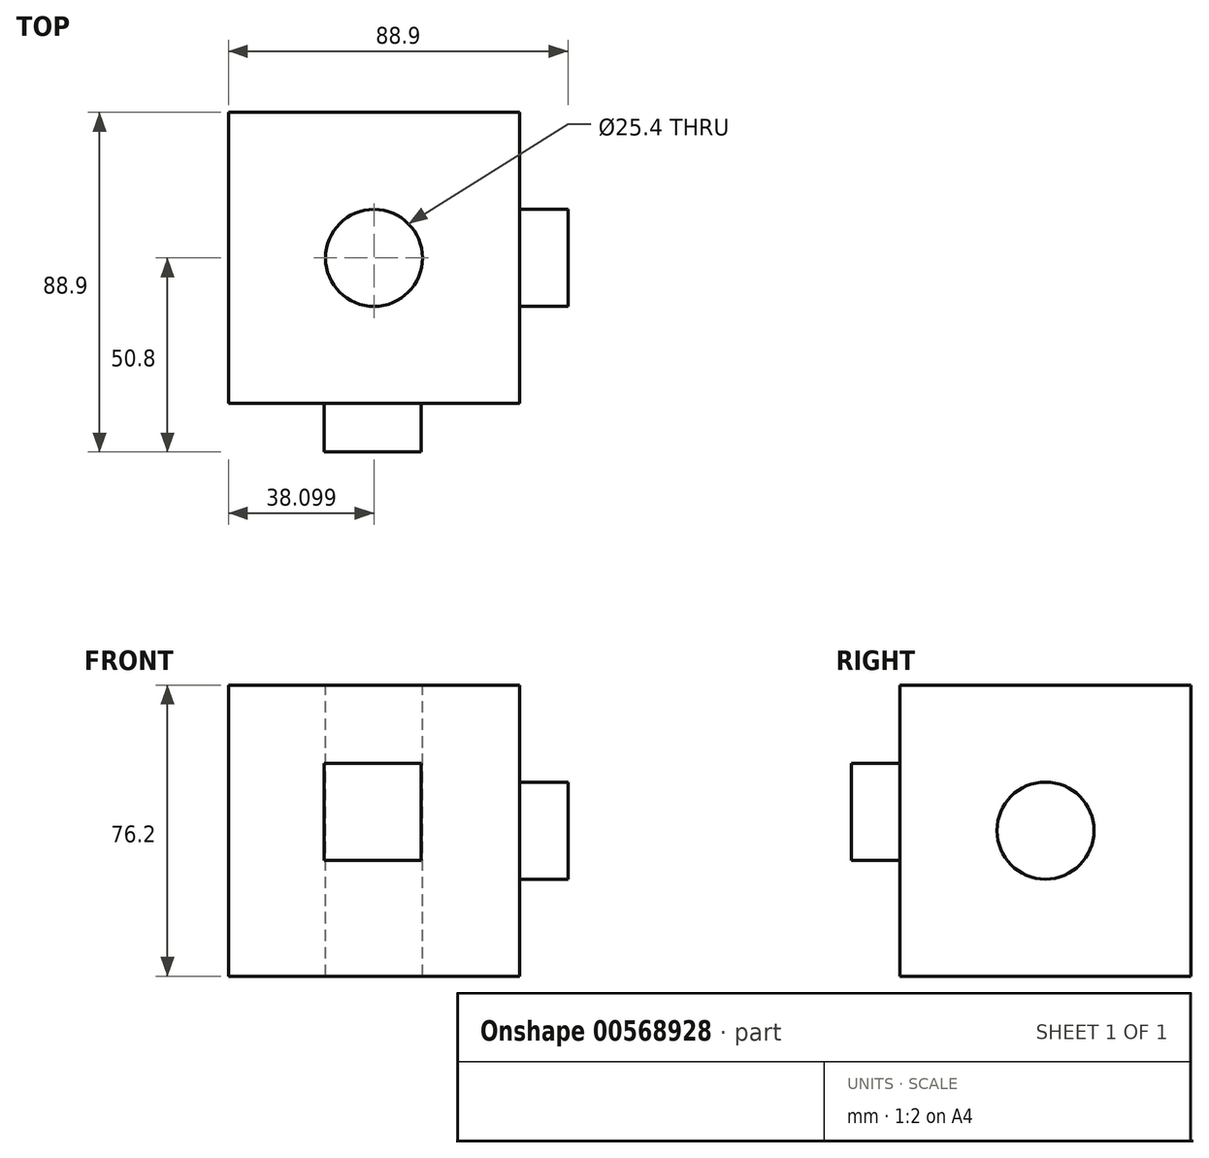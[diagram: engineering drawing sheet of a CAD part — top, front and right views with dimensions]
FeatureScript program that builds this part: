
annotation { "Feature Type Name" : "Feature", "Feature Type Description" : "" }
export const myFeature = defineFeature(function(context is Context, id is Id, definition is map)
    precondition{}
    {
        {
            var Q0;
            Q0=qCreatedBy(makeId("Front.planeOp"),FACE);
            var sketch = newSketch(context, id + "F0", { "sketchPlane" : qUnion([Q0])});
            skLineSegment(sketch, "E0.bottom", {"start": v(76.3, 85.32) * mm, "end": v(0.1, 85.32) * mm});
            skLineSegment(sketch, "E0.top", {"start": v(76.3, 9.12) * mm, "end": v(0.1, 9.12) * mm});
            skLineSegment(sketch, "E0.left", {"start": v(76.3, 85.32) * mm, "end": v(76.3, 9.12) * mm});
            skLineSegment(sketch, "E0.right", {"start": v(0.1, 85.32) * mm, "end": v(0.1, 9.12) * mm});
            skSolve(sketch);
        }
        {
            var Q0;
            Q0=makeQuery(id+"F0.imprint","IMPRINT",FACE,{"disambiguationData":[TD([[makeQuery(id+"F0.imprint","IMPRINT",EDGE,{"derivedFrom":sQuery(id+"F0.wireOp",EDGE,"E0.bottom")}),1.0]])]});
            extrude(context, id + "F1", {"entities" : qUnion([Q0]), "depth" : 76.2 * mm, "offsetDistance" : 25.4 * mm});
        }
        {
            var Q0;
            Q0=makeQuery(id+"F1.opExtrude","SWEPT_FACE",FACE,{"disambiguationData":[OSD([sQuery(id+"F0.wireOp",EDGE,"E0.bottom")])]});
            var sketch = newSketch(context, id + "F2", { "sketchPlane" : qUnion([Q0])});
            skPoint(sketch, "E1", {"position": v(38.2, -38.1) * mm});
            skSolve(sketch);
        }
        {
            var Q0;
            Q0=sQuery(id+"F2.wireOp",VERTEX,"E1");
            var Q1;
            Q1=makeQuery(id+"F1.opExtrude","SWEPT_BODY",BODY,{"disambiguationData":[OSD([sQuery(id+"F0.wireOp",EDGE,"E0.bottom"),sQuery(id+"F0.wireOp",EDGE,"E0.top"),sQuery(id+"F0.wireOp",EDGE,"E0.left"),sQuery(id+"F0.wireOp",EDGE,"E0.right")])]});
            hole(context, id + "F3", {"style" : HoleStyle.SIMPLE, "endStyle" : HoleEndStyle.THROUGH, "holeDiameter" : 25.4 * mm, "isTappedThrough" : true, "tappedDepth" : 12.7 * mm, "tapClearance" : 3, "locations" : qUnion([Q0]), "scope" : qUnion([Q1])});
        }
        {
            var Q0;
            Q0=makeQuery(id+"F1.opExtrude","CAP_FACE",FACE,{"disambiguationData":[OSD([sQuery(id+"F0.wireOp",EDGE,"E0.bottom"),sQuery(id+"F0.wireOp",EDGE,"E0.top"),sQuery(id+"F0.wireOp",EDGE,"E0.left"),sQuery(id+"F0.wireOp",EDGE,"E0.right")])],"isStart":false});
            var sketch = newSketch(context, id + "F4", { "sketchPlane" : qUnion([Q0])});
            skPoint(sketch, "E2", {"position": v(38.2, 47.22) * mm});
            skSolve(sketch);
        }
        {
            var Q0;
            Q0=makeQuery(id+"F4.imprint","IMPRINT",FACE,{"disambiguationData":[TD([[makeQuery(id+"F4.imprint","IMPRINT",EDGE,{"derivedFrom":makeQuery(id+"F1.opExtrude","CAP_EDGE",EDGE,{"disambiguationData":[OSD([sQuery(id+"F0.wireOp",EDGE,"E0.bottom")])],"isStart":false})}),1.0]])]});
            var sketch = newSketch(context, id + "F5", { "sketchPlane" : qUnion([Q0])});
            skLineSegment(sketch, "E3.bottom", {"start": v(25.18, 64.81) * mm, "end": v(50.58, 64.81) * mm});
            skLineSegment(sketch, "E3.top", {"start": v(25.18, 39.41) * mm, "end": v(50.58, 39.41) * mm});
            skLineSegment(sketch, "E3.left", {"start": v(25.18, 64.81) * mm, "end": v(25.18, 39.41) * mm});
            skLineSegment(sketch, "E3.right", {"start": v(50.58, 64.81) * mm, "end": v(50.58, 39.41) * mm});
            skSolve(sketch);
        }
        {
            var Q0;
            Q0=makeQuery(id+"F5.imprint","IMPRINT",FACE,{"disambiguationData":[TD([[makeQuery(id+"F5.imprint","IMPRINT",EDGE,{"derivedFrom":sQuery(id+"F5.wireOp",EDGE,"E3.bottom")}),-1.0]])]});
            extrude(context, id + "F6", {"entities" : qUnion([Q0]), "operationType" : NewBodyOperationType.ADD, "depth" : 12.7 * mm, "offsetDistance" : 25.4 * mm});
        }
        {
            var Q0;
            Q0=makeQuery(id+"F1.opExtrude","SWEPT_FACE",FACE,{"disambiguationData":[OSD([sQuery(id+"F0.wireOp",EDGE,"E0.left")])]});
            var sketch = newSketch(context, id + "F7", { "sketchPlane" : qUnion([Q0])});
            skPoint(sketch, "E4", {"position": v(-38.1, 47.22) * mm});
            skCircle(sketch, "E5", {"center": v(-38.1, 47.22) * mm, "radius": 12.7 * mm});
            skSolve(sketch);
        }
        {
            var Q0;
            Q0=makeQuery(id+"F7.imprint","IMPRINT",FACE,{"disambiguationData":[TD([[makeQuery(id+"F7.imprint","IMPRINT",EDGE,{"derivedFrom":sQuery(id+"F7.wireOp",EDGE,"E5")}),1.0]])]});
            extrude(context, id + "F8", {"entities" : qUnion([Q0]), "operationType" : NewBodyOperationType.ADD, "depth" : 12.7 * mm, "offsetDistance" : 25.4 * mm});
        }
    });
